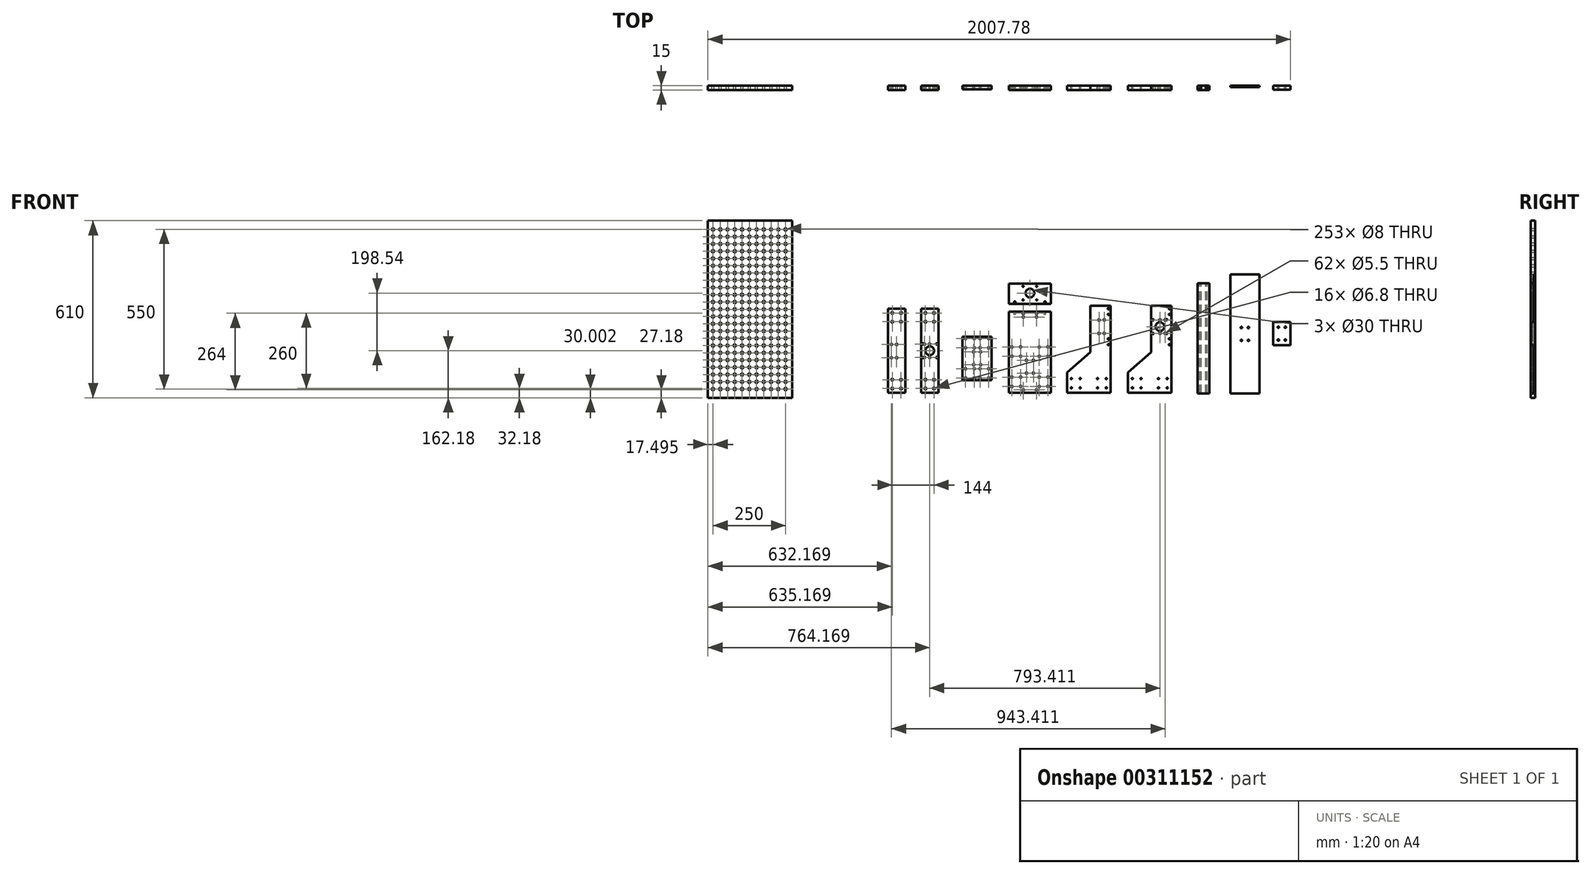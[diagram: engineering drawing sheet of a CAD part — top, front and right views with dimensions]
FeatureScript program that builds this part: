
annotation { "Feature Type Name" : "Feature", "Feature Type Description" : "" }
export const myFeature = defineFeature(function(context is Context, id is Id, definition is map)
    precondition{}
    {
        {
            var Q0;
            Q0=qCreatedBy(makeId("Front.planeOp"),FACE);
            var sketch = newSketch(context, id + "F0", { "sketchPlane" : qUnion([Q0])});
            skLineSegment(sketch, "E0.top", {"start": v(-80, -122) * mm, "end": v(70, -122) * mm});
            skLineSegment(sketch, "E0.right", {"start": v(70, 178) * mm, "end": v(70, -122) * mm});
            skCircle(sketch, "E1", {"center": v(-65, -73) * mm, "radius": 2.1 * mm});
            skCircle(sketch, "E2", {"center": v(-35, -73) * mm, "radius": 2.1 * mm});
            skCircle(sketch, "E3", {"center": v(-65, -105) * mm, "radius": 2.1 * mm});
            skCircle(sketch, "E4", {"center": v(-35, -105) * mm, "radius": 2.1 * mm});
            skCircle(sketch, "E5", {"center": v(25, -73) * mm, "radius": 2.1 * mm});
            skCircle(sketch, "E6", {"center": v(55, -73) * mm, "radius": 2.1 * mm});
            skCircle(sketch, "E7", {"center": v(25, -105) * mm, "radius": 2.1 * mm});
            skCircle(sketch, "E8", {"center": v(55, -105) * mm, "radius": 2.1 * mm});
            skLineSegment(sketch, "E9.bottom", {"start": v(160, 255.6) * mm, "end": v(200, 255.6) * mm});
            skLineSegment(sketch, "E9.top", {"start": v(160, -124.4) * mm, "end": v(200, -124.4) * mm});
            skLineSegment(sketch, "E9.left", {"start": v(160, 255.6) * mm, "end": v(160, -124.4) * mm});
            skLineSegment(sketch, "E9.right", {"start": v(200, 255.6) * mm, "end": v(200, -124.4) * mm});
            skLineSegment(sketch, "E10.bottom", {"start": v(272.74, 285.6) * mm, "end": v(372.74, 285.6) * mm});
            skLineSegment(sketch, "E10.top", {"start": v(272.74, -124.4) * mm, "end": v(372.74, -124.4) * mm});
            skLineSegment(sketch, "E10.left", {"start": v(272.74, 285.6) * mm, "end": v(272.74, -124.4) * mm});
            skLineSegment(sketch, "E10.right", {"start": v(372.74, 285.6) * mm, "end": v(372.74, -124.4) * mm});
            skLineSegment(sketch, "E11", {"start": v(-80, -52) * mm, "end": v(0, 18) * mm});
            skLineSegment(sketch, "E12", {"start": v(0, 18) * mm, "end": v(0, 178) * mm});
            skLineSegment(sketch, "E13", {"start": v(-80, -122) * mm, "end": v(-80, -52) * mm});
            skLineSegment(sketch, "E14", {"start": v(0, 178) * mm, "end": v(70, 178) * mm});
            skCircle(sketch, "E15", {"center": v(30, 106) * mm, "radius": 15 * mm});
            skLineSegment(sketch, "E16.bottom", {"start": v(-346, -122) * mm, "end": v(-490, -122) * mm});
            skLineSegment(sketch, "E16.top", {"start": v(-346, 158) * mm, "end": v(-490, 158) * mm});
            skLineSegment(sketch, "E16.left", {"start": v(-346, -122) * mm, "end": v(-346, 158) * mm});
            skLineSegment(sketch, "E16.right", {"start": v(-490, -122) * mm, "end": v(-490, 158) * mm});
            skLineSegment(sketch, "E17", {"start": v(-418, 81.5) * mm, "end": v(-418, -101.19) * mm, "construction": true});
            skPoint(sketch, "E17.startSnap0", {"position": v(-418, 158) * mm});
            skPoint(sketch, "E18.startSnap0", {"position": v(-490, 18) * mm});
            skCircle(sketch, "E19", {"center": v(-480, 36) * mm, "radius": 2.75 * mm});
            skCircle(sketch, "E20", {"center": v(-450, 36) * mm, "radius": 2.75 * mm});
            skCircle(sketch, "E21", {"center": v(-450, 4) * mm, "radius": 2.75 * mm});
            skCircle(sketch, "E22", {"center": v(-480, 4) * mm, "radius": 2.75 * mm});
            skCircle(sketch, "E23.MirrorC", {"center": v(-356, 36) * mm, "radius": 2.75 * mm});
            skCircle(sketch, "E24.MirrorC", {"center": v(-386, 36) * mm, "radius": 2.75 * mm});
            skCircle(sketch, "E25.MirrorC", {"center": v(-356, 4) * mm, "radius": 2.75 * mm});
            skCircle(sketch, "E26.MirrorC", {"center": v(-386, 4) * mm, "radius": 2.75 * mm});
            skCircle(sketch, "E27", {"center": v(-430, -10) * mm, "radius": 2.75 * mm});
            skCircle(sketch, "E28.MirrorC", {"center": v(-406, -10) * mm, "radius": 2.75 * mm});
            skLineSegment(sketch, "E29", {"start": v(285.64, 80.6) * mm, "end": v(355.09, 80.6) * mm, "construction": true});
            skPoint(sketch, "E29.startSnap0", {"position": v(272.74, 80.6) * mm});
            skLineSegment(sketch, "E30", {"start": v(322.74, 119.41) * mm, "end": v(322.74, 27.5) * mm, "construction": true});
            skPoint(sketch, "E30.startSnap0", {"position": v(322.74, 285.6) * mm});
            skCircle(sketch, "E31", {"center": v(310.74, 102.6) * mm, "radius": 2.5 * mm});
            skCircle(sketch, "E32.MirrorC", {"center": v(334.74, 102.6) * mm, "radius": 2.5 * mm});
            skCircle(sketch, "E33.MirrorC", {"center": v(310.74, 58.6) * mm, "radius": 2.5 * mm});
            skCircle(sketch, "E34.MirrorC", {"center": v(334.74, 58.6) * mm, "radius": 2.5 * mm});
            skLineSegment(sketch, "E35.bottom", {"start": v(420.2, 121.75) * mm, "end": v(480.2, 121.75) * mm});
            skLineSegment(sketch, "E35.top", {"start": v(420.2, 41.75) * mm, "end": v(480.2, 41.75) * mm});
            skLineSegment(sketch, "E35.left", {"start": v(420.2, 121.75) * mm, "end": v(420.2, 41.75) * mm});
            skLineSegment(sketch, "E35.right", {"start": v(480.2, 121.75) * mm, "end": v(480.2, 41.75) * mm});
            skLineSegment(sketch, "E36", {"start": v(450.2, 101.17) * mm, "end": v(450.2, 65.59) * mm, "construction": true});
            skPoint(sketch, "E36.startSnap0", {"position": v(450.2, 121.75) * mm});
            skLineSegment(sketch, "E37", {"start": v(471.52, 81.75) * mm, "end": v(432.14, 81.75) * mm, "construction": true});
            skPoint(sketch, "E37.startSnap0", {"position": v(480.2, 81.75) * mm});
            skCircle(sketch, "E38", {"center": v(438.2, 103.75) * mm, "radius": 2.5 * mm});
            skCircle(sketch, "E39.MirrorC", {"center": v(462.2, 103.75) * mm, "radius": 2.5 * mm});
            skCircle(sketch, "E40.MirrorC", {"center": v(438.2, 59.75) * mm, "radius": 2.5 * mm});
            skCircle(sketch, "E41.MirrorC", {"center": v(462.2, 59.75) * mm, "radius": 2.5 * mm});
            skLineSegment(sketch, "E42", {"start": v(-442.15, -32) * mm, "end": v(-396.47, -32) * mm, "construction": true});
            skLineSegment(sketch, "E43.bottom", {"start": v(-550, -78.17) * mm, "end": v(-650, -78.17) * mm});
            skLineSegment(sketch, "E43.top", {"start": v(-550, 71.83) * mm, "end": v(-650, 71.83) * mm});
            skLineSegment(sketch, "E43.left", {"start": v(-550, -78.17) * mm, "end": v(-550, 71.83) * mm});
            skLineSegment(sketch, "E43.right", {"start": v(-650, -78.17) * mm, "end": v(-650, 71.83) * mm});
            skLineSegment(sketch, "E44", {"start": v(-600, 83.24) * mm, "end": v(-600, -99.44) * mm, "construction": true});
            skPoint(sketch, "E45.startSnap0", {"position": v(-509.97, 18.83) * mm});
            skCircle(sketch, "E46", {"center": v(-640, 64.83) * mm, "radius": 2.75 * mm});
            skCircle(sketch, "E47", {"center": v(-610, 64.83) * mm, "radius": 2.75 * mm});
            skCircle(sketch, "E48", {"center": v(-610, 32.83) * mm, "radius": 2.75 * mm});
            skCircle(sketch, "E49", {"center": v(-640, 32.83) * mm, "radius": 2.75 * mm});
            skCircle(sketch, "E50.MirrorC", {"center": v(-560, 64.83) * mm, "radius": 2.75 * mm});
            skCircle(sketch, "E51.MirrorC", {"center": v(-590, 64.83) * mm, "radius": 2.75 * mm});
            skCircle(sketch, "E52.MirrorC", {"center": v(-560, 32.83) * mm, "radius": 2.75 * mm});
            skCircle(sketch, "E53.MirrorC", {"center": v(-590, 32.83) * mm, "radius": 2.75 * mm});
            skCircle(sketch, "E54", {"center": v(-612, 18.83) * mm, "radius": 2.75 * mm});
            skCircle(sketch, "E55.MirrorC", {"center": v(-588, 18.83) * mm, "radius": 2.75 * mm});
            skLineSegment(sketch, "E56", {"start": v(-612.15, -3.17) * mm, "end": v(-566.47, -3.17) * mm, "construction": true});
            skCircle(sketch, "E57.MirrorC", {"center": v(-610, -71.17) * mm, "radius": 2.75 * mm});
            skCircle(sketch, "E58.MirrorC", {"center": v(-640, -71.17) * mm, "radius": 2.75 * mm});
            skCircle(sketch, "E59.MirrorC", {"center": v(-640, -39.17) * mm, "radius": 2.75 * mm});
            skCircle(sketch, "E60.MirrorC", {"center": v(-610, -39.17) * mm, "radius": 2.75 * mm});
            skCircle(sketch, "E61.MirrorC", {"center": v(-612, -25.17) * mm, "radius": 2.75 * mm});
            skCircle(sketch, "E62.MirrorC", {"center": v(-560, -71.17) * mm, "radius": 2.75 * mm});
            skCircle(sketch, "E63.MirrorC", {"center": v(-590, -71.17) * mm, "radius": 2.75 * mm});
            skCircle(sketch, "E64.MirrorC", {"center": v(-560, -39.17) * mm, "radius": 2.75 * mm});
            skCircle(sketch, "E65.MirrorC", {"center": v(-588, -25.17) * mm, "radius": 2.75 * mm});
            skCircle(sketch, "E66.MirrorC", {"center": v(-590, -39.17) * mm, "radius": 2.75 * mm});
            skCircle(sketch, "E67.MirrorC", {"center": v(-480, -68) * mm, "radius": 2.75 * mm});
            skCircle(sketch, "E68.MirrorC", {"center": v(-450, -100) * mm, "radius": 2.75 * mm});
            skPoint(sketch, "E69.MirrorP", {"position": v(-490, -82) * mm});
            skCircle(sketch, "E70.MirrorC", {"center": v(-450, -68) * mm, "radius": 2.75 * mm});
            skCircle(sketch, "E71.MirrorC", {"center": v(-430, -54) * mm, "radius": 2.75 * mm});
            skCircle(sketch, "E72.MirrorC", {"center": v(-480, -100) * mm, "radius": 2.75 * mm});
            skCircle(sketch, "E73.MirrorC", {"center": v(-356, -68) * mm, "radius": 2.75 * mm});
            skCircle(sketch, "E74.MirrorC", {"center": v(-386, -100) * mm, "radius": 2.75 * mm});
            skCircle(sketch, "E75.MirrorC", {"center": v(-356, -100) * mm, "radius": 2.75 * mm});
            skCircle(sketch, "E76.MirrorC", {"center": v(-406, -54) * mm, "radius": 2.75 * mm});
            skCircle(sketch, "E77.MirrorC", {"center": v(-386, -68) * mm, "radius": 2.75 * mm});
            skLineSegment(sketch, "E78.top", {"start": v(-290, -122) * mm, "end": v(-140, -122) * mm});
            skLineSegment(sketch, "E78.right", {"start": v(-140, 178) * mm, "end": v(-140, -122) * mm});
            skCircle(sketch, "E79", {"center": v(-275, -73) * mm, "radius": 2.1 * mm});
            skCircle(sketch, "E80", {"center": v(-245, -73) * mm, "radius": 2.1 * mm});
            skCircle(sketch, "E81", {"center": v(-275, -105) * mm, "radius": 2.1 * mm});
            skCircle(sketch, "E82", {"center": v(-245, -105) * mm, "radius": 2.1 * mm});
            skCircle(sketch, "E83", {"center": v(-185, -73) * mm, "radius": 2.1 * mm});
            skCircle(sketch, "E84", {"center": v(-155, -73) * mm, "radius": 2.1 * mm});
            skCircle(sketch, "E85", {"center": v(-185, -105) * mm, "radius": 2.1 * mm});
            skCircle(sketch, "E86", {"center": v(-155, -105) * mm, "radius": 2.1 * mm});
            skLineSegment(sketch, "E87", {"start": v(-290, -52) * mm, "end": v(-210, 18) * mm});
            skLineSegment(sketch, "E88", {"start": v(-210, 18) * mm, "end": v(-210, 178) * mm});
            skLineSegment(sketch, "E89", {"start": v(-290, -122) * mm, "end": v(-290, -52) * mm});
            skLineSegment(sketch, "E90", {"start": v(-210, 178) * mm, "end": v(-140, 178) * mm});
            skCircle(sketch, "E91", {"center": v(-162, 129) * mm, "radius": 2.75 * mm});
            skCircle(sketch, "E92", {"center": v(-180, 129) * mm, "radius": 2.75 * mm});
            skCircle(sketch, "E93", {"center": v(-162, 83) * mm, "radius": 2.75 * mm});
            skCircle(sketch, "E94", {"center": v(-180, 83) * mm, "radius": 2.75 * mm});
            skCircle(sketch, "E95", {"center": v(48, 129) * mm, "radius": 2.75 * mm});
            skCircle(sketch, "E96", {"center": v(30, 129) * mm, "radius": 2.75 * mm});
            skCircle(sketch, "E97", {"center": v(48, 83) * mm, "radius": 2.75 * mm});
            skCircle(sketch, "E98", {"center": v(30, 83) * mm, "radius": 2.75 * mm});
            skCircle(sketch, "E99", {"center": v(62.5, 168) * mm, "radius": 2.25 * mm});
            skCircle(sketch, "E100", {"center": v(62.5, 148) * mm, "radius": 2.25 * mm});
            skCircle(sketch, "E101", {"center": v(-147.5, 168) * mm, "radius": 2.25 * mm});
            skCircle(sketch, "E102", {"center": v(-147.5, 148) * mm, "radius": 2.25 * mm});
            skCircle(sketch, "E103", {"center": v(62.5, 64) * mm, "radius": 2.25 * mm});
            skCircle(sketch, "E104", {"center": v(62.5, 44) * mm, "radius": 2.25 * mm});
            skCircle(sketch, "E105", {"center": v(-147.5, 64) * mm, "radius": 2.25 * mm});
            skCircle(sketch, "E106", {"center": v(-147.5, 44) * mm, "radius": 2.25 * mm});
            skCircle(sketch, "E107", {"center": v(-441, 152) * mm, "radius": 2.75 * mm});
            skCircle(sketch, "E108", {"center": v(-395, 152) * mm, "radius": 2.75 * mm});
            skCircle(sketch, "E109", {"center": v(-441, 139) * mm, "radius": 2.75 * mm});
            skCircle(sketch, "E110", {"center": v(-395, 139) * mm, "radius": 2.75 * mm});
            skCircle(sketch, "E111", {"center": v(-441, -112) * mm, "radius": 2.75 * mm});
            skCircle(sketch, "E112", {"center": v(-395, -112) * mm, "radius": 2.75 * mm});
            skLineSegment(sketch, "E113.bottom", {"start": v(-733.41, -122) * mm, "end": v(-793.41, -122) * mm});
            skLineSegment(sketch, "E113.top", {"start": v(-733.41, 168) * mm, "end": v(-793.41, 168) * mm});
            skLineSegment(sketch, "E113.left", {"start": v(-733.41, -122) * mm, "end": v(-733.41, 168) * mm});
            skLineSegment(sketch, "E113.right", {"start": v(-793.41, -122) * mm, "end": v(-793.41, 168) * mm});
            skLineSegment(sketch, "E114", {"start": v(-724.9, 23) * mm, "end": v(-713.92, 23) * mm, "construction": true});
            skPoint(sketch, "E114.startSnap0", {"position": v(-733.41, 23) * mm});
            skPoint(sketch, "E114.endSnap0", {"position": v(-733.41, 23) * mm});
            skCircle(sketch, "E115", {"center": v(-763.41, 46) * mm, "radius": 2.75 * mm});
            skCircle(sketch, "E116", {"center": v(-781.41, 46) * mm, "radius": 2.75 * mm});
            skCircle(sketch, "E117", {"center": v(-763.41, 0) * mm, "radius": 2.75 * mm});
            skCircle(sketch, "E118", {"center": v(-781.41, 0) * mm, "radius": 2.75 * mm});
            skCircle(sketch, "E119", {"center": v(-778.41, 153) * mm, "radius": 3.4 * mm});
            skCircle(sketch, "E120", {"center": v(-748.41, 153) * mm, "radius": 3.4 * mm});
            skCircle(sketch, "E121", {"center": v(-778.41, 123) * mm, "radius": 3.4 * mm});
            skCircle(sketch, "E122", {"center": v(-748.41, 123) * mm, "radius": 3.4 * mm});
            skCircle(sketch, "E123.MirrorC", {"center": v(-748.41, -77) * mm, "radius": 3.4 * mm});
            skCircle(sketch, "E124.MirrorC", {"center": v(-748.41, -107) * mm, "radius": 3.4 * mm});
            skCircle(sketch, "E125.MirrorC", {"center": v(-778.41, -107) * mm, "radius": 3.4 * mm});
            skCircle(sketch, "E126.MirrorC", {"center": v(-778.41, -77) * mm, "radius": 3.4 * mm});
            skLineSegment(sketch, "E127.bottom", {"start": v(-847.41, -122) * mm, "end": v(-907.41, -122) * mm});
            skLineSegment(sketch, "E127.top", {"start": v(-847.41, 168) * mm, "end": v(-907.41, 168) * mm});
            skLineSegment(sketch, "E127.left", {"start": v(-847.41, -122) * mm, "end": v(-847.41, 168) * mm});
            skLineSegment(sketch, "E127.right", {"start": v(-907.41, -122) * mm, "end": v(-907.41, 168) * mm});
            skLineSegment(sketch, "E128", {"start": v(-838.9, 23) * mm, "end": v(-827.92, 23) * mm, "construction": true});
            skPoint(sketch, "E128.startSnap0", {"position": v(-847.41, 23) * mm});
            skPoint(sketch, "E128.endSnap0", {"position": v(-847.41, 23) * mm});
            skCircle(sketch, "E129", {"center": v(-877.41, 44.72) * mm, "radius": 2.75 * mm});
            skCircle(sketch, "E130", {"center": v(-895.41, 44.72) * mm, "radius": 2.75 * mm});
            skCircle(sketch, "E131", {"center": v(-877.41, -1.28) * mm, "radius": 2.75 * mm});
            skCircle(sketch, "E132", {"center": v(-895.41, -1.28) * mm, "radius": 2.75 * mm});
            skCircle(sketch, "E133", {"center": v(-892.41, 153) * mm, "radius": 3.4 * mm});
            skCircle(sketch, "E134", {"center": v(-862.41, 153) * mm, "radius": 3.4 * mm});
            skCircle(sketch, "E135", {"center": v(-892.41, 123) * mm, "radius": 3.4 * mm});
            skCircle(sketch, "E136", {"center": v(-862.41, 123) * mm, "radius": 3.4 * mm});
            skCircle(sketch, "E137.MirrorC", {"center": v(-862.41, -77) * mm, "radius": 3.4 * mm});
            skCircle(sketch, "E138.MirrorC", {"center": v(-862.41, -107) * mm, "radius": 3.4 * mm});
            skCircle(sketch, "E139.MirrorC", {"center": v(-892.41, -107) * mm, "radius": 3.4 * mm});
            skCircle(sketch, "E140.MirrorC", {"center": v(-892.41, -77) * mm, "radius": 3.4 * mm});
            skCircle(sketch, "E141", {"center": v(-763.41, 23) * mm, "radius": 15 * mm});
            skCircle(sketch, "E142", {"center": v(-786.91, 46.5) * mm, "radius": 2 * mm});
            skCircle(sketch, "E143", {"center": v(-786.91, -0.5) * mm, "radius": 2 * mm});
            skCircle(sketch, "E144", {"center": v(-739.91, 46.5) * mm, "radius": 2 * mm});
            skCircle(sketch, "E145", {"center": v(-739.91, -0.5) * mm, "radius": 2 * mm});
            skCircle(sketch, "E146", {"center": v(6.5, 129.5) * mm, "radius": 2 * mm});
            skCircle(sketch, "E147", {"center": v(6.5, 82.5) * mm, "radius": 2 * mm});
            skCircle(sketch, "E148", {"center": v(53.5, 130.2) * mm, "radius": 2 * mm});
            skCircle(sketch, "E149", {"center": v(53.5, 82.5) * mm, "radius": 2 * mm});
            skLineSegment(sketch, "E150", {"start": v(-490, 184.54) * mm, "end": v(-346, 184.54) * mm});
            skLineSegment(sketch, "E151", {"start": v(-346, 184.54) * mm, "end": v(-346, 254.54) * mm});
            skLineSegment(sketch, "E152", {"start": v(-346, 254.54) * mm, "end": v(-490, 254.54) * mm});
            skLineSegment(sketch, "E153", {"start": v(-490, 254.54) * mm, "end": v(-490, 184.54) * mm});
            skCircle(sketch, "E154", {"center": v(-470, 190.54) * mm, "radius": 2.5 * mm});
            skCircle(sketch, "E155", {"center": v(-366, 190.54) * mm, "radius": 2.5 * mm});
            skCircle(sketch, "E156", {"center": v(-418, 221.54) * mm, "radius": 15 * mm});
            skPoint(sketch, "E156.centerSnap0", {"position": v(-418, 254.54) * mm});
            skCircle(sketch, "E157", {"center": v(-441.5, 245.04) * mm, "radius": 1.75 * mm});
            skCircle(sketch, "E158", {"center": v(-441.5, 198.04) * mm, "radius": 1.82 * mm});
            skCircle(sketch, "E159", {"center": v(-394.5, 198.04) * mm, "radius": 1.6 * mm});
            skCircle(sketch, "E160", {"center": v(-394.5, 245.04) * mm, "radius": 1.88 * mm});
            skLineSegment(sketch, "E161.bottom", {"start": v(-1527.58, 470.82) * mm, "end": v(-1237.58, 470.82) * mm});
            skLineSegment(sketch, "E161.top", {"start": v(-1527.58, -139.18) * mm, "end": v(-1237.58, -139.18) * mm});
            skLineSegment(sketch, "E161.left", {"start": v(-1527.58, 470.82) * mm, "end": v(-1527.58, -139.18) * mm});
            skLineSegment(sketch, "E161.right", {"start": v(-1237.58, 470.82) * mm, "end": v(-1237.58, -139.18) * mm});
            skCircle(sketch, "E162", {"center": v(-1510.08, -109.18) * mm, "radius": 4 * mm});
            skCircle(sketch, "E163.0.1.0", {"center": v(-1510.08, -84.18) * mm, "radius": 4 * mm});
            skCircle(sketch, "E163.0.2.0", {"center": v(-1510.08, -59.18) * mm, "radius": 4 * mm});
            skCircle(sketch, "E163.0.3.0", {"center": v(-1510.08, -34.18) * mm, "radius": 4 * mm});
            skCircle(sketch, "E163.0.4.0", {"center": v(-1510.08, -9.18) * mm, "radius": 4 * mm});
            skCircle(sketch, "E163.0.5.0", {"center": v(-1510.08, 15.82) * mm, "radius": 4 * mm});
            skCircle(sketch, "E163.0.6.0", {"center": v(-1510.08, 40.82) * mm, "radius": 4 * mm});
            skCircle(sketch, "E163.0.7.0", {"center": v(-1510.08, 65.82) * mm, "radius": 4 * mm});
            skCircle(sketch, "E163.0.8.0", {"center": v(-1510.08, 90.82) * mm, "radius": 4 * mm});
            skCircle(sketch, "E163.0.9.0", {"center": v(-1510.08, 115.82) * mm, "radius": 4 * mm});
            skCircle(sketch, "E163.0.10.0", {"center": v(-1510.08, 140.82) * mm, "radius": 4 * mm});
            skCircle(sketch, "E163.0.11.0", {"center": v(-1510.08, 165.82) * mm, "radius": 4 * mm});
            skCircle(sketch, "E163.0.12.0", {"center": v(-1510.08, 190.82) * mm, "radius": 4 * mm});
            skCircle(sketch, "E163.0.13.0", {"center": v(-1510.08, 215.82) * mm, "radius": 4 * mm});
            skCircle(sketch, "E163.0.14.0", {"center": v(-1510.08, 240.82) * mm, "radius": 4 * mm});
            skCircle(sketch, "E163.0.15.0", {"center": v(-1510.08, 265.82) * mm, "radius": 4 * mm});
            skCircle(sketch, "E163.0.16.0", {"center": v(-1510.08, 290.82) * mm, "radius": 4 * mm});
            skCircle(sketch, "E163.0.17.0", {"center": v(-1510.08, 315.82) * mm, "radius": 4 * mm});
            skCircle(sketch, "E163.0.18.0", {"center": v(-1510.08, 340.82) * mm, "radius": 4 * mm});
            skCircle(sketch, "E163.0.19.0", {"center": v(-1510.08, 365.82) * mm, "radius": 4 * mm});
            skCircle(sketch, "E163.0.20.0", {"center": v(-1510.08, 390.82) * mm, "radius": 4 * mm});
            skCircle(sketch, "E163.0.21.0", {"center": v(-1510.08, 415.82) * mm, "radius": 4 * mm});
            skCircle(sketch, "E163.0.22.0", {"center": v(-1510.08, 440.82) * mm, "radius": 4 * mm});
            skCircle(sketch, "E163.1.0.0", {"center": v(-1485.08, -109.18) * mm, "radius": 4 * mm});
            skCircle(sketch, "E163.1.1.0", {"center": v(-1485.08, -84.18) * mm, "radius": 4 * mm});
            skCircle(sketch, "E163.1.2.0", {"center": v(-1485.08, -59.18) * mm, "radius": 4 * mm});
            skCircle(sketch, "E163.1.3.0", {"center": v(-1485.08, -34.18) * mm, "radius": 4 * mm});
            skCircle(sketch, "E163.1.4.0", {"center": v(-1485.08, -9.18) * mm, "radius": 4 * mm});
            skCircle(sketch, "E163.1.5.0", {"center": v(-1485.08, 15.82) * mm, "radius": 4 * mm});
            skCircle(sketch, "E163.1.6.0", {"center": v(-1485.08, 40.82) * mm, "radius": 4 * mm});
            skCircle(sketch, "E163.1.7.0", {"center": v(-1485.08, 65.82) * mm, "radius": 4 * mm});
            skCircle(sketch, "E163.1.8.0", {"center": v(-1485.08, 90.82) * mm, "radius": 4 * mm});
            skCircle(sketch, "E163.1.9.0", {"center": v(-1485.08, 115.82) * mm, "radius": 4 * mm});
            skCircle(sketch, "E163.1.10.0", {"center": v(-1485.08, 140.82) * mm, "radius": 4 * mm});
            skCircle(sketch, "E163.1.11.0", {"center": v(-1485.08, 165.82) * mm, "radius": 4 * mm});
            skCircle(sketch, "E163.1.12.0", {"center": v(-1485.08, 190.82) * mm, "radius": 4 * mm});
            skCircle(sketch, "E163.1.13.0", {"center": v(-1485.08, 215.82) * mm, "radius": 4 * mm});
            skCircle(sketch, "E163.1.14.0", {"center": v(-1485.08, 240.82) * mm, "radius": 4 * mm});
            skCircle(sketch, "E163.1.15.0", {"center": v(-1485.08, 265.82) * mm, "radius": 4 * mm});
            skCircle(sketch, "E163.1.16.0", {"center": v(-1485.08, 290.82) * mm, "radius": 4 * mm});
            skCircle(sketch, "E163.1.17.0", {"center": v(-1485.08, 315.82) * mm, "radius": 4 * mm});
            skCircle(sketch, "E163.1.18.0", {"center": v(-1485.08, 340.82) * mm, "radius": 4 * mm});
            skCircle(sketch, "E163.1.19.0", {"center": v(-1485.08, 365.82) * mm, "radius": 4 * mm});
            skCircle(sketch, "E163.1.20.0", {"center": v(-1485.08, 390.82) * mm, "radius": 4 * mm});
            skCircle(sketch, "E163.1.21.0", {"center": v(-1485.08, 415.82) * mm, "radius": 4 * mm});
            skCircle(sketch, "E163.1.22.0", {"center": v(-1485.08, 440.82) * mm, "radius": 4 * mm});
            skCircle(sketch, "E163.2.0.0", {"center": v(-1460.08, -109.18) * mm, "radius": 4 * mm});
            skCircle(sketch, "E163.2.1.0", {"center": v(-1460.08, -84.18) * mm, "radius": 4 * mm});
            skCircle(sketch, "E163.2.2.0", {"center": v(-1460.08, -59.18) * mm, "radius": 4 * mm});
            skCircle(sketch, "E163.2.3.0", {"center": v(-1460.08, -34.18) * mm, "radius": 4 * mm});
            skCircle(sketch, "E163.2.4.0", {"center": v(-1460.08, -9.18) * mm, "radius": 4 * mm});
            skCircle(sketch, "E163.2.5.0", {"center": v(-1460.08, 15.82) * mm, "radius": 4 * mm});
            skCircle(sketch, "E163.2.6.0", {"center": v(-1460.08, 40.82) * mm, "radius": 4 * mm});
            skCircle(sketch, "E163.2.7.0", {"center": v(-1460.08, 65.82) * mm, "radius": 4 * mm});
            skCircle(sketch, "E163.2.8.0", {"center": v(-1460.08, 90.82) * mm, "radius": 4 * mm});
            skCircle(sketch, "E163.2.9.0", {"center": v(-1460.08, 115.82) * mm, "radius": 4 * mm});
            skCircle(sketch, "E163.2.10.0", {"center": v(-1460.08, 140.82) * mm, "radius": 4 * mm});
            skCircle(sketch, "E163.2.11.0", {"center": v(-1460.08, 165.82) * mm, "radius": 4 * mm});
            skCircle(sketch, "E163.2.12.0", {"center": v(-1460.08, 190.82) * mm, "radius": 4 * mm});
            skCircle(sketch, "E163.2.13.0", {"center": v(-1460.08, 215.82) * mm, "radius": 4 * mm});
            skCircle(sketch, "E163.2.14.0", {"center": v(-1460.08, 240.82) * mm, "radius": 4 * mm});
            skCircle(sketch, "E163.2.15.0", {"center": v(-1460.08, 265.82) * mm, "radius": 4 * mm});
            skCircle(sketch, "E163.2.16.0", {"center": v(-1460.08, 290.82) * mm, "radius": 4 * mm});
            skCircle(sketch, "E163.2.17.0", {"center": v(-1460.08, 315.82) * mm, "radius": 4 * mm});
            skCircle(sketch, "E163.2.18.0", {"center": v(-1460.08, 340.82) * mm, "radius": 4 * mm});
            skCircle(sketch, "E163.2.19.0", {"center": v(-1460.08, 365.82) * mm, "radius": 4 * mm});
            skCircle(sketch, "E163.2.20.0", {"center": v(-1460.08, 390.82) * mm, "radius": 4 * mm});
            skCircle(sketch, "E163.2.21.0", {"center": v(-1460.08, 415.82) * mm, "radius": 4 * mm});
            skCircle(sketch, "E163.2.22.0", {"center": v(-1460.08, 440.82) * mm, "radius": 4 * mm});
            skCircle(sketch, "E163.3.0.0", {"center": v(-1435.08, -109.18) * mm, "radius": 4 * mm});
            skCircle(sketch, "E163.3.1.0", {"center": v(-1435.08, -84.18) * mm, "radius": 4 * mm});
            skCircle(sketch, "E163.3.2.0", {"center": v(-1435.08, -59.18) * mm, "radius": 4 * mm});
            skCircle(sketch, "E163.3.3.0", {"center": v(-1435.08, -34.18) * mm, "radius": 4 * mm});
            skCircle(sketch, "E163.3.4.0", {"center": v(-1435.08, -9.18) * mm, "radius": 4 * mm});
            skCircle(sketch, "E163.3.5.0", {"center": v(-1435.08, 15.82) * mm, "radius": 4 * mm});
            skCircle(sketch, "E163.3.6.0", {"center": v(-1435.08, 40.82) * mm, "radius": 4 * mm});
            skCircle(sketch, "E163.3.7.0", {"center": v(-1435.08, 65.82) * mm, "radius": 4 * mm});
            skCircle(sketch, "E163.3.8.0", {"center": v(-1435.08, 90.82) * mm, "radius": 4 * mm});
            skCircle(sketch, "E163.3.9.0", {"center": v(-1435.08, 115.82) * mm, "radius": 4 * mm});
            skCircle(sketch, "E163.3.10.0", {"center": v(-1435.08, 140.82) * mm, "radius": 4 * mm});
            skCircle(sketch, "E163.3.11.0", {"center": v(-1435.08, 165.82) * mm, "radius": 4 * mm});
            skCircle(sketch, "E163.3.12.0", {"center": v(-1435.08, 190.82) * mm, "radius": 4 * mm});
            skCircle(sketch, "E163.3.13.0", {"center": v(-1435.08, 215.82) * mm, "radius": 4 * mm});
            skCircle(sketch, "E163.3.14.0", {"center": v(-1435.08, 240.82) * mm, "radius": 4 * mm});
            skCircle(sketch, "E163.3.15.0", {"center": v(-1435.08, 265.82) * mm, "radius": 4 * mm});
            skCircle(sketch, "E163.3.16.0", {"center": v(-1435.08, 290.82) * mm, "radius": 4 * mm});
            skCircle(sketch, "E163.3.17.0", {"center": v(-1435.08, 315.82) * mm, "radius": 4 * mm});
            skCircle(sketch, "E163.3.18.0", {"center": v(-1435.08, 340.82) * mm, "radius": 4 * mm});
            skCircle(sketch, "E163.3.19.0", {"center": v(-1435.08, 365.82) * mm, "radius": 4 * mm});
            skCircle(sketch, "E163.3.20.0", {"center": v(-1435.08, 390.82) * mm, "radius": 4 * mm});
            skCircle(sketch, "E163.3.21.0", {"center": v(-1435.08, 415.82) * mm, "radius": 4 * mm});
            skCircle(sketch, "E163.3.22.0", {"center": v(-1435.08, 440.82) * mm, "radius": 4 * mm});
            skCircle(sketch, "E163.4.0.0", {"center": v(-1410.08, -109.18) * mm, "radius": 4 * mm});
            skCircle(sketch, "E163.4.1.0", {"center": v(-1410.08, -84.18) * mm, "radius": 4 * mm});
            skCircle(sketch, "E163.4.2.0", {"center": v(-1410.08, -59.18) * mm, "radius": 4 * mm});
            skCircle(sketch, "E163.4.3.0", {"center": v(-1410.08, -34.18) * mm, "radius": 4 * mm});
            skCircle(sketch, "E163.4.4.0", {"center": v(-1410.08, -9.18) * mm, "radius": 4 * mm});
            skCircle(sketch, "E163.4.5.0", {"center": v(-1410.08, 15.82) * mm, "radius": 4 * mm});
            skCircle(sketch, "E163.4.6.0", {"center": v(-1410.08, 40.82) * mm, "radius": 4 * mm});
            skCircle(sketch, "E163.4.7.0", {"center": v(-1410.08, 65.82) * mm, "radius": 4 * mm});
            skCircle(sketch, "E163.4.8.0", {"center": v(-1410.08, 90.82) * mm, "radius": 4 * mm});
            skCircle(sketch, "E163.4.9.0", {"center": v(-1410.08, 115.82) * mm, "radius": 4 * mm});
            skCircle(sketch, "E163.4.10.0", {"center": v(-1410.08, 140.82) * mm, "radius": 4 * mm});
            skCircle(sketch, "E163.4.11.0", {"center": v(-1410.08, 165.82) * mm, "radius": 4 * mm});
            skCircle(sketch, "E163.4.12.0", {"center": v(-1410.08, 190.82) * mm, "radius": 4 * mm});
            skCircle(sketch, "E163.4.13.0", {"center": v(-1410.08, 215.82) * mm, "radius": 4 * mm});
            skCircle(sketch, "E163.4.14.0", {"center": v(-1410.08, 240.82) * mm, "radius": 4 * mm});
            skCircle(sketch, "E163.4.15.0", {"center": v(-1410.08, 265.82) * mm, "radius": 4 * mm});
            skCircle(sketch, "E163.4.16.0", {"center": v(-1410.08, 290.82) * mm, "radius": 4 * mm});
            skCircle(sketch, "E163.4.17.0", {"center": v(-1410.08, 315.82) * mm, "radius": 4 * mm});
            skCircle(sketch, "E163.4.18.0", {"center": v(-1410.08, 340.82) * mm, "radius": 4 * mm});
            skCircle(sketch, "E163.4.19.0", {"center": v(-1410.08, 365.82) * mm, "radius": 4 * mm});
            skCircle(sketch, "E163.4.20.0", {"center": v(-1410.08, 390.82) * mm, "radius": 4 * mm});
            skCircle(sketch, "E163.4.21.0", {"center": v(-1410.08, 415.82) * mm, "radius": 4 * mm});
            skCircle(sketch, "E163.4.22.0", {"center": v(-1410.08, 440.82) * mm, "radius": 4 * mm});
            skCircle(sketch, "E163.5.0.0", {"center": v(-1385.08, -109.18) * mm, "radius": 4 * mm});
            skCircle(sketch, "E163.5.1.0", {"center": v(-1385.08, -84.18) * mm, "radius": 4 * mm});
            skCircle(sketch, "E163.5.2.0", {"center": v(-1385.08, -59.18) * mm, "radius": 4 * mm});
            skCircle(sketch, "E163.5.3.0", {"center": v(-1385.08, -34.18) * mm, "radius": 4 * mm});
            skCircle(sketch, "E163.5.4.0", {"center": v(-1385.08, -9.18) * mm, "radius": 4 * mm});
            skCircle(sketch, "E163.5.5.0", {"center": v(-1385.08, 15.82) * mm, "radius": 4 * mm});
            skCircle(sketch, "E163.5.6.0", {"center": v(-1385.08, 40.82) * mm, "radius": 4 * mm});
            skCircle(sketch, "E163.5.7.0", {"center": v(-1385.08, 65.82) * mm, "radius": 4 * mm});
            skCircle(sketch, "E163.5.8.0", {"center": v(-1385.08, 90.82) * mm, "radius": 4 * mm});
            skCircle(sketch, "E163.5.9.0", {"center": v(-1385.08, 115.82) * mm, "radius": 4 * mm});
            skCircle(sketch, "E163.5.10.0", {"center": v(-1385.08, 140.82) * mm, "radius": 4 * mm});
            skCircle(sketch, "E163.5.11.0", {"center": v(-1385.08, 165.82) * mm, "radius": 4 * mm});
            skCircle(sketch, "E163.5.12.0", {"center": v(-1385.08, 190.82) * mm, "radius": 4 * mm});
            skCircle(sketch, "E163.5.13.0", {"center": v(-1385.08, 215.82) * mm, "radius": 4 * mm});
            skCircle(sketch, "E163.5.14.0", {"center": v(-1385.08, 240.82) * mm, "radius": 4 * mm});
            skCircle(sketch, "E163.5.15.0", {"center": v(-1385.08, 265.82) * mm, "radius": 4 * mm});
            skCircle(sketch, "E163.5.16.0", {"center": v(-1385.08, 290.82) * mm, "radius": 4 * mm});
            skCircle(sketch, "E163.5.17.0", {"center": v(-1385.08, 315.82) * mm, "radius": 4 * mm});
            skCircle(sketch, "E163.5.18.0", {"center": v(-1385.08, 340.82) * mm, "radius": 4 * mm});
            skCircle(sketch, "E163.5.19.0", {"center": v(-1385.08, 365.82) * mm, "radius": 4 * mm});
            skCircle(sketch, "E163.5.20.0", {"center": v(-1385.08, 390.82) * mm, "radius": 4 * mm});
            skCircle(sketch, "E163.5.21.0", {"center": v(-1385.08, 415.82) * mm, "radius": 4 * mm});
            skCircle(sketch, "E163.5.22.0", {"center": v(-1385.08, 440.82) * mm, "radius": 4 * mm});
            skCircle(sketch, "E163.6.0.0", {"center": v(-1360.08, -109.18) * mm, "radius": 4 * mm});
            skCircle(sketch, "E163.6.1.0", {"center": v(-1360.08, -84.18) * mm, "radius": 4 * mm});
            skCircle(sketch, "E163.6.2.0", {"center": v(-1360.08, -59.18) * mm, "radius": 4 * mm});
            skCircle(sketch, "E163.6.3.0", {"center": v(-1360.08, -34.18) * mm, "radius": 4 * mm});
            skCircle(sketch, "E163.6.4.0", {"center": v(-1360.08, -9.18) * mm, "radius": 4 * mm});
            skCircle(sketch, "E163.6.5.0", {"center": v(-1360.08, 15.82) * mm, "radius": 4 * mm});
            skCircle(sketch, "E163.6.6.0", {"center": v(-1360.08, 40.82) * mm, "radius": 4 * mm});
            skCircle(sketch, "E163.6.7.0", {"center": v(-1360.08, 65.82) * mm, "radius": 4 * mm});
            skCircle(sketch, "E163.6.8.0", {"center": v(-1360.08, 90.82) * mm, "radius": 4 * mm});
            skCircle(sketch, "E163.6.9.0", {"center": v(-1360.08, 115.82) * mm, "radius": 4 * mm});
            skCircle(sketch, "E163.6.10.0", {"center": v(-1360.08, 140.82) * mm, "radius": 4 * mm});
            skCircle(sketch, "E163.6.11.0", {"center": v(-1360.08, 165.82) * mm, "radius": 4 * mm});
            skCircle(sketch, "E163.6.12.0", {"center": v(-1360.08, 190.82) * mm, "radius": 4 * mm});
            skCircle(sketch, "E163.6.13.0", {"center": v(-1360.08, 215.82) * mm, "radius": 4 * mm});
            skCircle(sketch, "E163.6.14.0", {"center": v(-1360.08, 240.82) * mm, "radius": 4 * mm});
            skCircle(sketch, "E163.6.15.0", {"center": v(-1360.08, 265.82) * mm, "radius": 4 * mm});
            skCircle(sketch, "E163.6.16.0", {"center": v(-1360.08, 290.82) * mm, "radius": 4 * mm});
            skCircle(sketch, "E163.6.17.0", {"center": v(-1360.08, 315.82) * mm, "radius": 4 * mm});
            skCircle(sketch, "E163.6.18.0", {"center": v(-1360.08, 340.82) * mm, "radius": 4 * mm});
            skCircle(sketch, "E163.6.19.0", {"center": v(-1360.08, 365.82) * mm, "radius": 4 * mm});
            skCircle(sketch, "E163.6.20.0", {"center": v(-1360.08, 390.82) * mm, "radius": 4 * mm});
            skCircle(sketch, "E163.6.21.0", {"center": v(-1360.08, 415.82) * mm, "radius": 4 * mm});
            skCircle(sketch, "E163.6.22.0", {"center": v(-1360.08, 440.82) * mm, "radius": 4 * mm});
            skCircle(sketch, "E163.7.0.0", {"center": v(-1335.08, -109.18) * mm, "radius": 4 * mm});
            skCircle(sketch, "E163.7.1.0", {"center": v(-1335.08, -84.18) * mm, "radius": 4 * mm});
            skCircle(sketch, "E163.7.2.0", {"center": v(-1335.08, -59.18) * mm, "radius": 4 * mm});
            skCircle(sketch, "E163.7.3.0", {"center": v(-1335.08, -34.18) * mm, "radius": 4 * mm});
            skCircle(sketch, "E163.7.4.0", {"center": v(-1335.08, -9.18) * mm, "radius": 4 * mm});
            skCircle(sketch, "E163.7.5.0", {"center": v(-1335.08, 15.82) * mm, "radius": 4 * mm});
            skCircle(sketch, "E163.7.6.0", {"center": v(-1335.08, 40.82) * mm, "radius": 4 * mm});
            skCircle(sketch, "E163.7.7.0", {"center": v(-1335.08, 65.82) * mm, "radius": 4 * mm});
            skCircle(sketch, "E163.7.8.0", {"center": v(-1335.08, 90.82) * mm, "radius": 4 * mm});
            skCircle(sketch, "E163.7.9.0", {"center": v(-1335.08, 115.82) * mm, "radius": 4 * mm});
            skCircle(sketch, "E163.7.10.0", {"center": v(-1335.08, 140.82) * mm, "radius": 4 * mm});
            skCircle(sketch, "E163.7.11.0", {"center": v(-1335.08, 165.82) * mm, "radius": 4 * mm});
            skCircle(sketch, "E163.7.12.0", {"center": v(-1335.08, 190.82) * mm, "radius": 4 * mm});
            skCircle(sketch, "E163.7.13.0", {"center": v(-1335.08, 215.82) * mm, "radius": 4 * mm});
            skCircle(sketch, "E163.7.14.0", {"center": v(-1335.08, 240.82) * mm, "radius": 4 * mm});
            skCircle(sketch, "E163.7.15.0", {"center": v(-1335.08, 265.82) * mm, "radius": 4 * mm});
            skCircle(sketch, "E163.7.16.0", {"center": v(-1335.08, 290.82) * mm, "radius": 4 * mm});
            skCircle(sketch, "E163.7.17.0", {"center": v(-1335.08, 315.82) * mm, "radius": 4 * mm});
            skCircle(sketch, "E163.7.18.0", {"center": v(-1335.08, 340.82) * mm, "radius": 4 * mm});
            skCircle(sketch, "E163.7.19.0", {"center": v(-1335.08, 365.82) * mm, "radius": 4 * mm});
            skCircle(sketch, "E163.7.20.0", {"center": v(-1335.08, 390.82) * mm, "radius": 4 * mm});
            skCircle(sketch, "E163.7.21.0", {"center": v(-1335.08, 415.82) * mm, "radius": 4 * mm});
            skCircle(sketch, "E163.7.22.0", {"center": v(-1335.08, 440.82) * mm, "radius": 4 * mm});
            skCircle(sketch, "E163.8.0.0", {"center": v(-1310.08, -109.18) * mm, "radius": 4 * mm});
            skCircle(sketch, "E163.8.1.0", {"center": v(-1310.08, -84.18) * mm, "radius": 4 * mm});
            skCircle(sketch, "E163.8.2.0", {"center": v(-1310.08, -59.18) * mm, "radius": 4 * mm});
            skCircle(sketch, "E163.8.3.0", {"center": v(-1310.08, -34.18) * mm, "radius": 4 * mm});
            skCircle(sketch, "E163.8.4.0", {"center": v(-1310.08, -9.18) * mm, "radius": 4 * mm});
            skCircle(sketch, "E163.8.5.0", {"center": v(-1310.08, 15.82) * mm, "radius": 4 * mm});
            skCircle(sketch, "E163.8.6.0", {"center": v(-1310.08, 40.82) * mm, "radius": 4 * mm});
            skCircle(sketch, "E163.8.7.0", {"center": v(-1310.08, 65.82) * mm, "radius": 4 * mm});
            skCircle(sketch, "E163.8.8.0", {"center": v(-1310.08, 90.82) * mm, "radius": 4 * mm});
            skCircle(sketch, "E163.8.9.0", {"center": v(-1310.08, 115.82) * mm, "radius": 4 * mm});
            skCircle(sketch, "E163.8.10.0", {"center": v(-1310.08, 140.82) * mm, "radius": 4 * mm});
            skCircle(sketch, "E163.8.11.0", {"center": v(-1310.08, 165.82) * mm, "radius": 4 * mm});
            skCircle(sketch, "E163.8.12.0", {"center": v(-1310.08, 190.82) * mm, "radius": 4 * mm});
            skCircle(sketch, "E163.8.13.0", {"center": v(-1310.08, 215.82) * mm, "radius": 4 * mm});
            skCircle(sketch, "E163.8.14.0", {"center": v(-1310.08, 240.82) * mm, "radius": 4 * mm});
            skCircle(sketch, "E163.8.15.0", {"center": v(-1310.08, 265.82) * mm, "radius": 4 * mm});
            skCircle(sketch, "E163.8.16.0", {"center": v(-1310.08, 290.82) * mm, "radius": 4 * mm});
            skCircle(sketch, "E163.8.17.0", {"center": v(-1310.08, 315.82) * mm, "radius": 4 * mm});
            skCircle(sketch, "E163.8.18.0", {"center": v(-1310.08, 340.82) * mm, "radius": 4 * mm});
            skCircle(sketch, "E163.8.19.0", {"center": v(-1310.08, 365.82) * mm, "radius": 4 * mm});
            skCircle(sketch, "E163.8.20.0", {"center": v(-1310.08, 390.82) * mm, "radius": 4 * mm});
            skCircle(sketch, "E163.8.21.0", {"center": v(-1310.08, 415.82) * mm, "radius": 4 * mm});
            skCircle(sketch, "E163.8.22.0", {"center": v(-1310.08, 440.82) * mm, "radius": 4 * mm});
            skCircle(sketch, "E163.9.0.0", {"center": v(-1285.08, -109.18) * mm, "radius": 4 * mm});
            skCircle(sketch, "E163.9.1.0", {"center": v(-1285.08, -84.18) * mm, "radius": 4 * mm});
            skCircle(sketch, "E163.9.2.0", {"center": v(-1285.08, -59.18) * mm, "radius": 4 * mm});
            skCircle(sketch, "E163.9.3.0", {"center": v(-1285.08, -34.18) * mm, "radius": 4 * mm});
            skCircle(sketch, "E163.9.4.0", {"center": v(-1285.08, -9.18) * mm, "radius": 4 * mm});
            skCircle(sketch, "E163.9.5.0", {"center": v(-1285.08, 15.82) * mm, "radius": 4 * mm});
            skCircle(sketch, "E163.9.6.0", {"center": v(-1285.08, 40.82) * mm, "radius": 4 * mm});
            skCircle(sketch, "E163.9.7.0", {"center": v(-1285.08, 65.82) * mm, "radius": 4 * mm});
            skCircle(sketch, "E163.9.8.0", {"center": v(-1285.08, 90.82) * mm, "radius": 4 * mm});
            skCircle(sketch, "E163.9.9.0", {"center": v(-1285.08, 115.82) * mm, "radius": 4 * mm});
            skCircle(sketch, "E163.9.10.0", {"center": v(-1285.08, 140.82) * mm, "radius": 4 * mm});
            skCircle(sketch, "E163.9.11.0", {"center": v(-1285.08, 165.82) * mm, "radius": 4 * mm});
            skCircle(sketch, "E163.9.12.0", {"center": v(-1285.08, 190.82) * mm, "radius": 4 * mm});
            skCircle(sketch, "E163.9.13.0", {"center": v(-1285.08, 215.82) * mm, "radius": 4 * mm});
            skCircle(sketch, "E163.9.14.0", {"center": v(-1285.08, 240.82) * mm, "radius": 4 * mm});
            skCircle(sketch, "E163.9.15.0", {"center": v(-1285.08, 265.82) * mm, "radius": 4 * mm});
            skCircle(sketch, "E163.9.16.0", {"center": v(-1285.08, 290.82) * mm, "radius": 4 * mm});
            skCircle(sketch, "E163.9.17.0", {"center": v(-1285.08, 315.82) * mm, "radius": 4 * mm});
            skCircle(sketch, "E163.9.18.0", {"center": v(-1285.08, 340.82) * mm, "radius": 4 * mm});
            skCircle(sketch, "E163.9.19.0", {"center": v(-1285.08, 365.82) * mm, "radius": 4 * mm});
            skCircle(sketch, "E163.9.20.0", {"center": v(-1285.08, 390.82) * mm, "radius": 4 * mm});
            skCircle(sketch, "E163.9.21.0", {"center": v(-1285.08, 415.82) * mm, "radius": 4 * mm});
            skCircle(sketch, "E163.9.22.0", {"center": v(-1285.08, 440.82) * mm, "radius": 4 * mm});
            skCircle(sketch, "E163.10.0.0", {"center": v(-1260.08, -109.18) * mm, "radius": 4 * mm});
            skCircle(sketch, "E163.10.1.0", {"center": v(-1260.08, -84.18) * mm, "radius": 4 * mm});
            skCircle(sketch, "E163.10.2.0", {"center": v(-1260.08, -59.18) * mm, "radius": 4 * mm});
            skCircle(sketch, "E163.10.3.0", {"center": v(-1260.08, -34.18) * mm, "radius": 4 * mm});
            skCircle(sketch, "E163.10.4.0", {"center": v(-1260.08, -9.18) * mm, "radius": 4 * mm});
            skCircle(sketch, "E163.10.5.0", {"center": v(-1260.08, 15.82) * mm, "radius": 4 * mm});
            skCircle(sketch, "E163.10.6.0", {"center": v(-1260.08, 40.82) * mm, "radius": 4 * mm});
            skCircle(sketch, "E163.10.7.0", {"center": v(-1260.08, 65.82) * mm, "radius": 4 * mm});
            skCircle(sketch, "E163.10.8.0", {"center": v(-1260.08, 90.82) * mm, "radius": 4 * mm});
            skCircle(sketch, "E163.10.9.0", {"center": v(-1260.08, 115.82) * mm, "radius": 4 * mm});
            skCircle(sketch, "E163.10.10.0", {"center": v(-1260.08, 140.82) * mm, "radius": 4 * mm});
            skCircle(sketch, "E163.10.11.0", {"center": v(-1260.08, 165.82) * mm, "radius": 4 * mm});
            skCircle(sketch, "E163.10.12.0", {"center": v(-1260.08, 190.82) * mm, "radius": 4 * mm});
            skCircle(sketch, "E163.10.13.0", {"center": v(-1260.08, 215.82) * mm, "radius": 4 * mm});
            skCircle(sketch, "E163.10.14.0", {"center": v(-1260.08, 240.82) * mm, "radius": 4 * mm});
            skCircle(sketch, "E163.10.15.0", {"center": v(-1260.08, 265.82) * mm, "radius": 4 * mm});
            skCircle(sketch, "E163.10.16.0", {"center": v(-1260.08, 290.82) * mm, "radius": 4 * mm});
            skCircle(sketch, "E163.10.17.0", {"center": v(-1260.08, 315.82) * mm, "radius": 4 * mm});
            skCircle(sketch, "E163.10.18.0", {"center": v(-1260.08, 340.82) * mm, "radius": 4 * mm});
            skCircle(sketch, "E163.10.19.0", {"center": v(-1260.08, 365.82) * mm, "radius": 4 * mm});
            skCircle(sketch, "E163.10.20.0", {"center": v(-1260.08, 390.82) * mm, "radius": 4 * mm});
            skCircle(sketch, "E163.10.21.0", {"center": v(-1260.08, 415.82) * mm, "radius": 4 * mm});
            skCircle(sketch, "E163.10.22.0", {"center": v(-1260.08, 440.82) * mm, "radius": 4 * mm});
            skLineSegment(sketch, "E163.direction1", {"start": v(-1510.08, -109.18) * mm, "end": v(-1485.08, -109.18) * mm, "construction": true});
            skLineSegment(sketch, "E163.direction2", {"start": v(-1510.08, -109.18) * mm, "end": v(-1510.08, -84.18) * mm, "construction": true});
            skSolve(sketch);
        }
        {
            var Q0;
            Q0=makeQuery(id+"F0.imprint","IMPRINT",FACE,{"disambiguationData":[TD([[makeQuery(id+"F0.imprint","IMPRINT",EDGE,{"derivedFrom":sQuery(id+"F0.wireOp",EDGE,"E0.bottom")}),-1.0]])]});
            var Q1;
            Q1=makeQuery(id+"F0.imprint","IMPRINT",FACE,{"disambiguationData":[TD([[makeQuery(id+"F0.imprint","IMPRINT",EDGE,{"derivedFrom":sQuery(id+"F0.wireOp",EDGE,"E9.bottom")}),-1.0]])]});
            var Q2;
            Q2=makeQuery(id+"F0.imprint","IMPRINT",FACE,{"disambiguationData":[TD([[makeQuery(id+"F0.imprint","IMPRINT",EDGE,{"derivedFrom":sQuery(id+"F0.wireOp",EDGE,"E0.top")}),1.0]])]});
            var Q3;
            Q3=makeQuery(id+"F0.imprint","IMPRINT",FACE,{"disambiguationData":[TD([[makeQuery(id+"F0.imprint","IMPRINT",EDGE,{"derivedFrom":sQuery(id+"F0.wireOp",EDGE,"E78.top")}),1.0]])]});
            var Q4;
            Q4=makeQuery(id+"F0.imprint","IMPRINT",FACE,{"disambiguationData":[TD([[makeQuery(id+"F0.imprint","IMPRINT",EDGE,{"derivedFrom":sQuery(id+"F0.wireOp",EDGE,"E113.bottom")}),-1.0]])]});
            var Q5;
            Q5=makeQuery(id+"F0.imprint","IMPRINT",FACE,{"disambiguationData":[TD([[makeQuery(id+"F0.imprint","IMPRINT",EDGE,{"derivedFrom":sQuery(id+"F0.wireOp",EDGE,"E127.bottom")}),-1.0]])]});
            var Q6;
            Q6=makeQuery(id+"F0.imprint","IMPRINT",FACE,{"disambiguationData":[TD([[makeQuery(id+"F0.imprint","IMPRINT",EDGE,{"derivedFrom":sQuery(id+"F0.wireOp",EDGE,"4AFk4IOF-1ujA-UHFH-n2Ep-7u8ghfslvrqv")}),1.0]])]});
            var Q7;
            Q7=makeQuery(id+"F0.imprint","IMPRINT",FACE,{"disambiguationData":[TD([[makeQuery(id+"F0.imprint","IMPRINT",EDGE,{"derivedFrom":sQuery(id+"F0.wireOp",EDGE,"E150")}),1.0]])]});
            var Q8;
            Q8=makeQuery(id+"F0.imprint","IMPRINT",FACE,{"disambiguationData":[TD([[makeQuery(id+"F0.imprint","IMPRINT",EDGE,{"derivedFrom":sQuery(id+"F0.wireOp",EDGE,"E161.bottom")}),-1.0]])]});
            extrude(context, id + "F1", {"entities" : qUnion([Q0, Q1, Q2, Q3, Q4, Q5, Q6, Q7, Q8]), "depth" : 15 * mm});
        }
        {
            var Q0;
            Q0=makeQuery(id+"F0.imprint","IMPRINT",FACE,{"disambiguationData":[TD([[makeQuery(id+"F0.imprint","IMPRINT",EDGE,{"derivedFrom":sQuery(id+"F0.wireOp",EDGE,"E10.bottom")}),-1.0]])]});
            extrude(context, id + "F2", {"entities" : qUnion([Q0]), "depth" : 5 * mm});
        }
        {
            var Q0;
            Q0=makeQuery(id+"F0.imprint","IMPRINT",FACE,{"disambiguationData":[TD([[makeQuery(id+"F0.imprint","IMPRINT",EDGE,{"derivedFrom":sQuery(id+"F0.wireOp",EDGE,"E16.bottom")}),-1.0]])]});
            var Q1;
            Q1=makeQuery(id+"F0.imprint","IMPRINT",FACE,{"disambiguationData":[TD([[makeQuery(id+"F0.imprint","IMPRINT",EDGE,{"derivedFrom":sQuery(id+"F0.wireOp",EDGE,"E43.bottom")}),-1.0]])]});
            extrude(context, id + "F3", {"entities" : qUnion([Q0, Q1]), "depth" : 12 * mm});
        }
        {
            var Q0;
            Q0=makeQuery(id+"F0.imprint","IMPRINT",FACE,{"disambiguationData":[TD([[makeQuery(id+"F0.imprint","IMPRINT",EDGE,{"derivedFrom":sQuery(id+"F0.wireOp",EDGE,"E35.bottom")}),-1.0]])]});
            var Q1;
            Q1=makeQuery(id+"F0.imprint","IMPRINT",FACE,{"disambiguationData":[TD([[makeQuery(id+"F0.imprint","IMPRINT",EDGE,{"derivedFrom":sQuery(id+"F0.wireOp",EDGE,"fiKfg6HG-dRVA-gZ0J-CD8X-93dsFA0V2Esm.bottom")}),-1.0]])]});
            extrude(context, id + "F4", {"entities" : qUnion([Q0, Q1]), "depth" : 14 * mm});
        }
        {
            var Q0;
            Q0=makeQuery(id+"F1.opExtrude","SWEPT_FACE",FACE,{"disambiguationData":[OSD([sQuery(id+"F0.wireOp",EDGE,"E9.bottom")])]});
            var sketch = newSketch(context, id + "F5", { "sketchPlane" : qUnion([Q0])});
            skCircle(sketch, "E164", {"center": v(170, -7.5) * mm, "radius": 2.25 * mm});
            skPoint(sketch, "E164.centerSnap0", {"position": v(160, -7.5) * mm});
            skCircle(sketch, "E165", {"center": v(190, -7.5) * mm, "radius": 2.25 * mm});
            skSolve(sketch);
        }
        {
            var Q0;
            Q0=makeQuery(id+"F5.imprint","IMPRINT",FACE,{"disambiguationData":[TD([[makeQuery(id+"F5.imprint","IMPRINT",EDGE,{"derivedFrom":sQuery(id+"F5.wireOp",EDGE,"E164")}),1.0]])]});
            var Q1;
            Q1=makeQuery(id+"F5.imprint","IMPRINT",FACE,{"disambiguationData":[TD([[makeQuery(id+"F5.imprint","IMPRINT",EDGE,{"derivedFrom":sQuery(id+"F5.wireOp",EDGE,"E165")}),1.0]])]});
            extrude(context, id + "F6", {"entities" : qUnion([Q0, Q1]), "operationType" : NewBodyOperationType.REMOVE, "endBound" : BoundingType.THROUGH_ALL, "oppositeDirection" : true, "depth" : 25 * mm});
        }
        {
            var Q0;
            Q0=makeQuery(id+"F3.opExtrude","SWEPT_FACE",FACE,{"disambiguationData":[OSD([sQuery(id+"F0.wireOp",EDGE,"E16.top")])]});
            var sketch = newSketch(context, id + "F7", { "sketchPlane" : qUnion([Q0])});
            skCircle(sketch, "E166", {"center": v(-366, -6) * mm, "radius": 2.5 * mm});
            skPoint(sketch, "E166.centerSnap0", {"position": v(-346, -6) * mm});
            skCircle(sketch, "E167", {"center": v(-470, -6) * mm, "radius": 2.5 * mm});
            skPoint(sketch, "E167.centerSnap0", {"position": v(-490, -6) * mm});
            skSolve(sketch);
        }
        {
            var Q0;
            Q0=makeQuery(id+"F7.imprint","IMPRINT",FACE,{"disambiguationData":[TD([[makeQuery(id+"F7.imprint","IMPRINT",EDGE,{"derivedFrom":sQuery(id+"F7.wireOp",EDGE,"E167")}),1.0]])]});
            var Q1;
            Q1=makeQuery(id+"F7.imprint","IMPRINT",FACE,{"disambiguationData":[TD([[makeQuery(id+"F7.imprint","IMPRINT",EDGE,{"derivedFrom":sQuery(id+"F7.wireOp",EDGE,"E166")}),1.0]])]});
            extrude(context, id + "F8", {"entities" : qUnion([Q0, Q1]), "operationType" : NewBodyOperationType.REMOVE, "oppositeDirection" : true, "depth" : 10 * mm});
        }
    });
